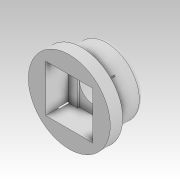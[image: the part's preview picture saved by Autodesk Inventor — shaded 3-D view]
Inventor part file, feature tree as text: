
AUTODESK INVENTOR PART (.ipt)
format: ipt  version: 2020 (Build 240168000, 168)  size: 161,280 bytes
history: native  units: mm
features: sketch x3, extrude x2, revolve x1, fillet x1, projected_geometry x1
ambient origin geometry x8: Origin, YZ Plane, XZ Plane, XY Plane, X Axis, Y Axis, Z Axis, Center Point
bodies: Solid1 (feature_tree)
feature tree (8):
  revolve  "Revolution1"  [1 undecoded]
  extrude  "Extrusion1"  Depth=1.5mm
  fillet  "Fillet1"  Radius=3.5mm
  extrude  "Extrusion2"  Depth=5.7mm
  sketch  "Sketch1"  dims[d0=1.7mm d1=3.95mm]
  sketch  "Sketch2"  dims[d2=1.0mm d3=1.5mm d4=3.5mm]
  sketch  "Sketch3"  dims[d5=90.0deg d6=5.7mm d7=2.7mm d8=0.0mm d9=0.5mm d10=0.2mm d11=0.0mm]
  projected_geometry  "Projected Loop1"
note: 1 required parameter value undecoded (feature->parameter linkage not recoverable at this tier; creation-order binding heuristic only, values carry confidence <= 0.55)
